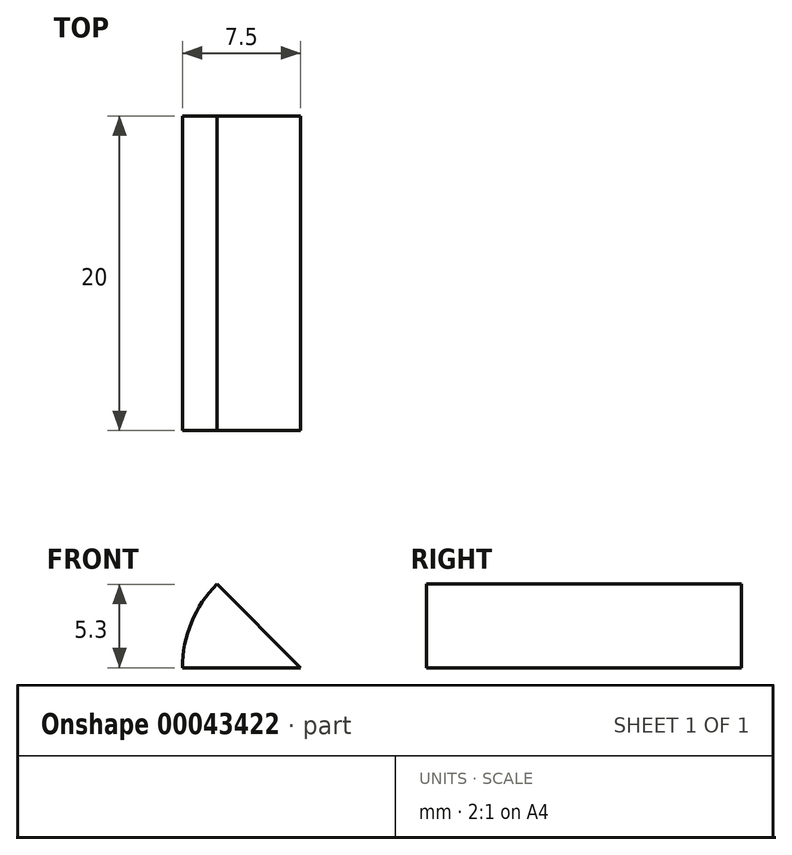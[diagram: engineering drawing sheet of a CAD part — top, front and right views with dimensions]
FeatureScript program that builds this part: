
annotation { "Feature Type Name" : "Feature", "Feature Type Description" : "" }
export const myFeature = defineFeature(function(context is Context, id is Id, definition is map)
    precondition{}
    {
        {
            var Q0;
            Q0=qCreatedBy(makeId("Front.planeOp"),FACE);
            var sketch = newSketch(context, id + "F0", { "sketchPlane" : qUnion([Q0])});
            skArc(sketch, "E0", {"start": v(-5.3, 5.3) * mm, "mid": v(-6.93, 2.87) * mm, "end": v(-7.5, 0) * mm});
            skLineSegment(sketch, "E1", {"start": v(-7.5, 0) * mm, "end": v(0, 0) * mm});
            skLineSegment(sketch, "E2", {"start": v(0, 0) * mm, "end": v(-5.3, 5.3) * mm});
            skPoint(sketch, "E3.orphan", {"position": v(0, 7.5) * mm});
            skSolve(sketch);
        }
        {
            var Q0;
            Q0=qSketchRegion(id+"F0",true);
            extrude(context, id + "F1", {"entities" : qUnion([Q0]), "depth" : 20 * mm});
        }
    });
